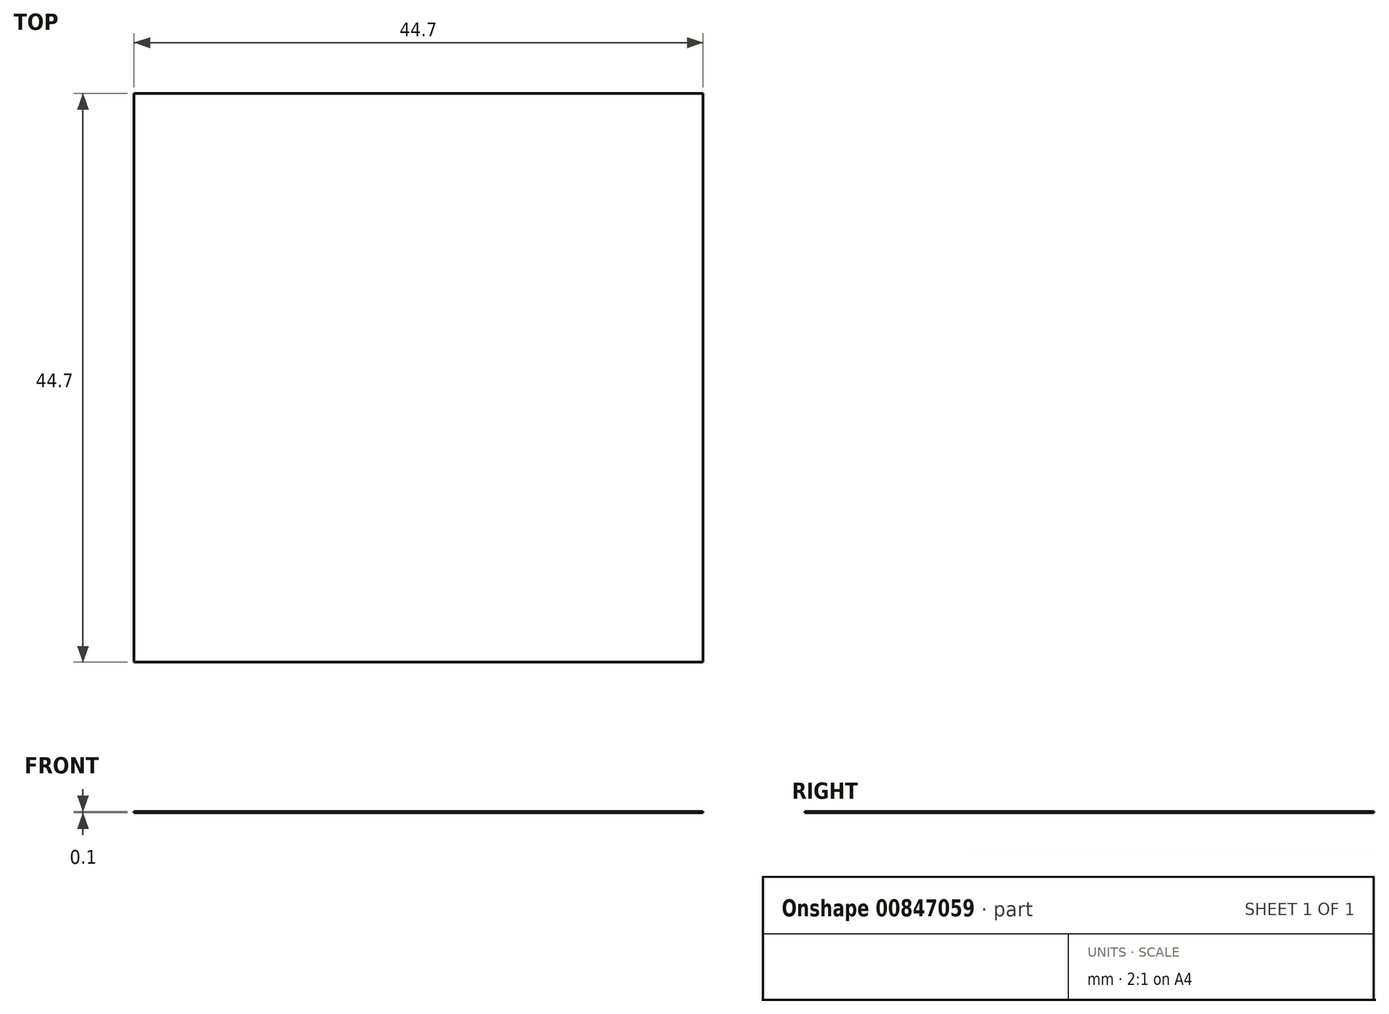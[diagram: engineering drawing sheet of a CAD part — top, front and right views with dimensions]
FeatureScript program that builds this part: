
annotation { "Feature Type Name" : "Feature", "Feature Type Description" : "" }
export const myFeature = defineFeature(function(context is Context, id is Id, definition is map)
    precondition{}
    {
        {
            var Q0;
            Q0=qCreatedBy(makeId("Top.planeOp"),FACE);
            var sketch = newSketch(context, id + "F0", { "sketchPlane" : qUnion([Q0])});
            skLineSegment(sketch, "E0.bottom", {"start": v(22.35, 22.35) * mm, "end": v(-22.35, 22.35) * mm});
            skLineSegment(sketch, "E0.top", {"start": v(22.35, -22.35) * mm, "end": v(-22.35, -22.35) * mm});
            skLineSegment(sketch, "E0.left", {"start": v(22.35, 22.35) * mm, "end": v(22.35, -22.35) * mm});
            skLineSegment(sketch, "E0.right", {"start": v(-22.35, 22.35) * mm, "end": v(-22.35, -22.35) * mm});
            skPoint(sketch, "E0.middle", {"position": v(0, 0) * mm});
            skSolve(sketch);
        }
        {
            var Q0;
            Q0=makeQuery(id+"F0.imprint","IMPRINT",FACE,{"disambiguationData":[TD([[makeQuery(id+"F0.imprint","IMPRINT",EDGE,{"derivedFrom":sQuery(id+"F0.wireOp",EDGE,"E0.bottom")}),1.0]])]});
            extrude(context, id + "F1", {"entities" : qUnion([Q0]), "depth" : .1 * mm, "offsetDistance" : 25 * mm});
        }
    });
